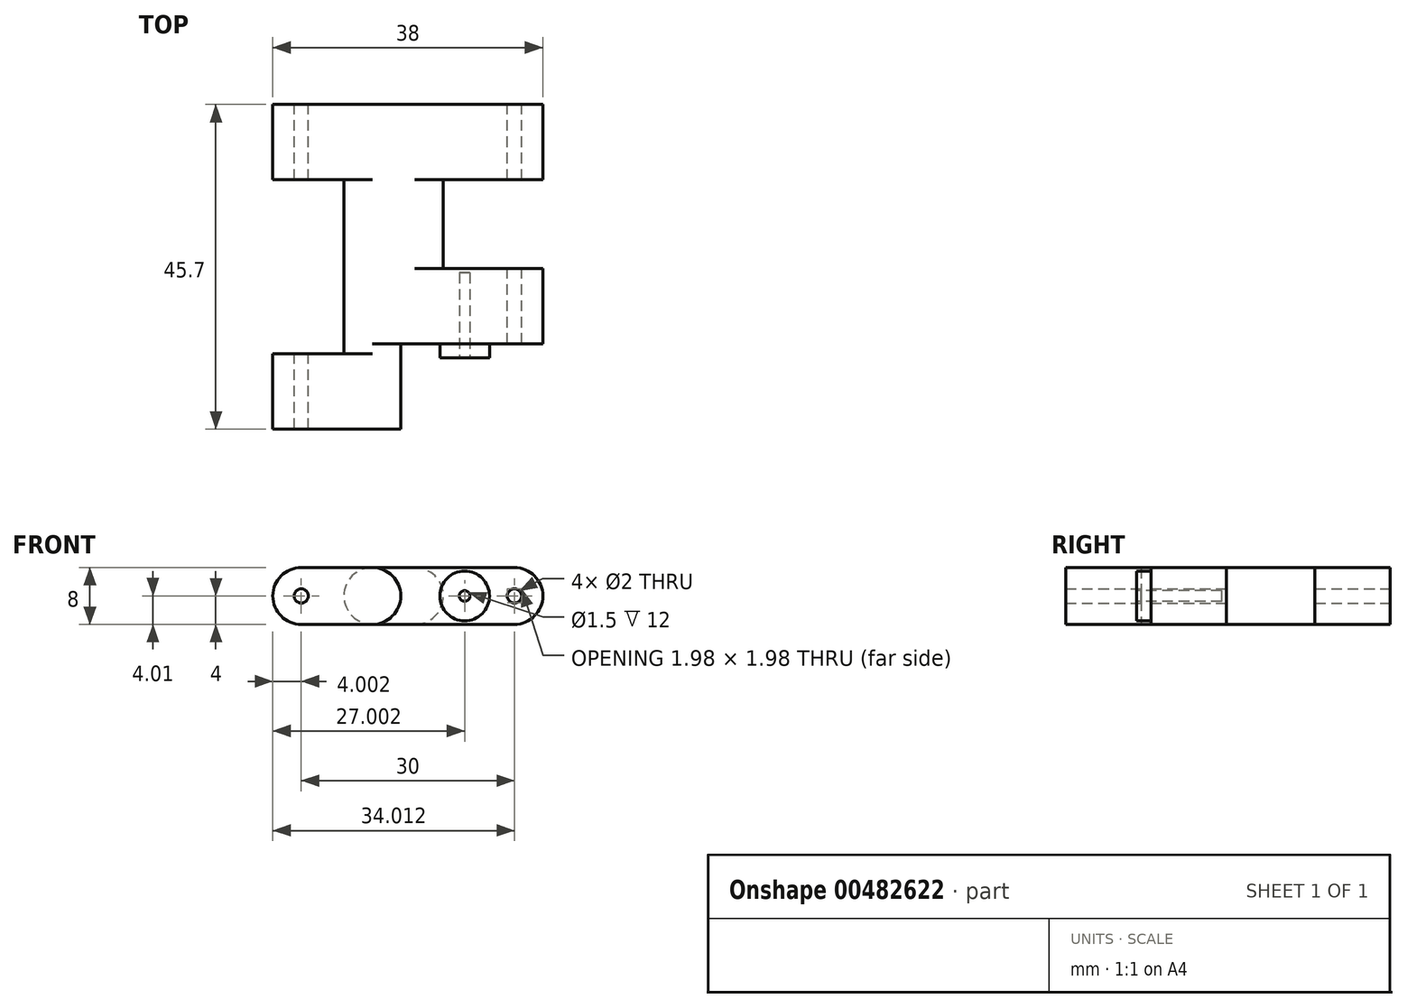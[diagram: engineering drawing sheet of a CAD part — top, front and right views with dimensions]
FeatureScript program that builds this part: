
annotation { "Feature Type Name" : "Feature", "Feature Type Description" : "" }
export const myFeature = defineFeature(function(context is Context, id is Id, definition is map)
    precondition{}
    {
        {
            var Q0;
            Q0=qCreatedBy(makeId("Top.planeOp"),FACE);
            var sketch = newSketch(context, id + "F0", { "sketchPlane" : qUnion([Q0])});
            skLineSegment(sketch, "E0", {"start": v(-9.9, -12.52) * mm, "end": v(8.1, -12.52) * mm});
            skLineSegment(sketch, "E1", {"start": v(8.1, -12.52) * mm, "end": v(8.1, -0.52) * mm});
            skLineSegment(sketch, "E2", {"start": v(8.1, -0.52) * mm, "end": v(28.1, -0.52) * mm});
            skLineSegment(sketch, "E3", {"start": v(28.1, -0.52) * mm, "end": v(28.1, 10.08) * mm});
            skLineSegment(sketch, "E4", {"start": v(28.1, 10.08) * mm, "end": v(14.1, 10.08) * mm});
            skLineSegment(sketch, "E5", {"start": v(14.1, 10.08) * mm, "end": v(14.1, 22.58) * mm});
            skLineSegment(sketch, "E6", {"start": v(14.1, 22.58) * mm, "end": v(28.1, 22.58) * mm});
            skLineSegment(sketch, "E7", {"start": v(28.1, 22.58) * mm, "end": v(28.1, 33.18) * mm});
            skLineSegment(sketch, "E8", {"start": v(28.1, 33.18) * mm, "end": v(-9.9, 33.18) * mm});
            skLineSegment(sketch, "E9", {"start": v(-9.9, 33.18) * mm, "end": v(-9.9, 22.58) * mm});
            skLineSegment(sketch, "E10", {"start": v(-9.9, 22.58) * mm, "end": v(0.1, 22.58) * mm});
            skLineSegment(sketch, "E11", {"start": v(0.1, 22.58) * mm, "end": v(0.1, -1.92) * mm});
            skLineSegment(sketch, "E12", {"start": v(0.1, -1.92) * mm, "end": v(-9.9, -1.92) * mm});
            skLineSegment(sketch, "E13", {"start": v(-9.9, -1.92) * mm, "end": v(-9.9, -12.52) * mm});
            skSolve(sketch);
        }
        {
            var Q0;
            Q0=makeQuery(id+"F0.imprint","IMPRINT",FACE,{"disambiguationData":[TD([[makeQuery(id+"F0.imprint","IMPRINT",EDGE,{"derivedFrom":sQuery(id+"F0.wireOp",EDGE,"E0")}),1.0]])]});
            extrude(context, id + "F1", {"entities" : qUnion([Q0]), "depth" : 8 * mm});
        }
        {
            var Q0;
            Q0=makeQuery(id+"F1.opExtrude","CAP_EDGE",EDGE,{"disambiguationData":[OSD([sQuery(id+"F0.wireOp",EDGE,"E13")])],"isStart":false});
            var Q1;
            Q1=makeQuery(id+"F1.opExtrude","CAP_EDGE",EDGE,{"disambiguationData":[OSD([sQuery(id+"F0.wireOp",EDGE,"E13")])],"isStart":true});
            var Q2;
            Q2=makeQuery(id+"F1.opExtrude","CAP_EDGE",EDGE,{"disambiguationData":[OSD([sQuery(id+"F0.wireOp",EDGE,"E1")])],"isStart":false});
            var Q3;
            Q3=makeQuery(id+"F1.opExtrude","CAP_EDGE",EDGE,{"disambiguationData":[OSD([sQuery(id+"F0.wireOp",EDGE,"E1")])],"isStart":true});
            var Q4;
            Q4=makeQuery(id+"F1.opExtrude","CAP_EDGE",EDGE,{"disambiguationData":[OSD([sQuery(id+"F0.wireOp",EDGE,"E3")])],"isStart":false});
            var Q5;
            Q5=makeQuery(id+"F1.opExtrude","CAP_EDGE",EDGE,{"disambiguationData":[OSD([sQuery(id+"F0.wireOp",EDGE,"E3")])],"isStart":true});
            var Q6;
            Q6=makeQuery(id+"F1.opExtrude","CAP_EDGE",EDGE,{"disambiguationData":[OSD([sQuery(id+"F0.wireOp",EDGE,"E7")])],"isStart":false});
            var Q7;
            Q7=makeQuery(id+"F1.opExtrude","CAP_EDGE",EDGE,{"disambiguationData":[OSD([sQuery(id+"F0.wireOp",EDGE,"E7")])],"isStart":true});
            var Q8;
            Q8=makeQuery(id+"F1.opExtrude","CAP_EDGE",EDGE,{"disambiguationData":[OSD([sQuery(id+"F0.wireOp",EDGE,"E9")])],"isStart":false});
            var Q9;
            Q9=makeQuery(id+"F1.opExtrude","CAP_EDGE",EDGE,{"disambiguationData":[OSD([sQuery(id+"F0.wireOp",EDGE,"E9")])],"isStart":true});
            fillet(context, id + "F2", {"entities" : qUnion([Q0, Q1, Q2, Q3, Q4, Q5, Q6, Q7, Q8, Q9]), "radius" : 4 * mm, "tangentPropagation" : true, "allowEdgeOverflow" : false});
        }
        {
            var Q0;
            Q0=makeQuery(id+"F1.opExtrude","SWEPT_FACE",FACE,{"disambiguationData":[OSD([sQuery(id+"F0.wireOp",EDGE,"E8")])]});
            var sketch = newSketch(context, id + "F3", { "sketchPlane" : qUnion([Q0])});
            skCircle(sketch, "E14", {"center": v(-24.1, 4) * mm, "radius": 1 * mm});
            skCircle(sketch, "E15", {"center": v(5.9, 4) * mm, "radius": 1 * mm});
            skSolve(sketch);
        }
        {
            var Q0;
            Q0 = qSketchRegion(id + "F3", true);
            extrude(context, id + "F4", {"entities" : qUnion([Q0]), "operationType" : NewBodyOperationType.REMOVE, "oppositeDirection" : true, "depth" : 60 * mm});
        }
        {
            var Q0;
            Q0=makeQuery(id+"F1.opExtrude","SWEPT_FACE",FACE,{"disambiguationData":[OSD([sQuery(id+"F0.wireOp",EDGE,"E2")])]});
            var sketch = newSketch(context, id + "F5", { "sketchPlane" : qUnion([Q0])});
            skCircle(sketch, "E16", {"center": v(17.1, 4) * mm, "radius": 3.5 * mm});
            skPoint(sketch, "E16.centerSnap0", {"position": v(28.1, 4) * mm});
            skSolve(sketch);
        }
        {
            var Q0;
            Q0=makeQuery(id+"F1.opExtrude","CAP_EDGE",EDGE,{"disambiguationData":[OSD([sQuery(id+"F0.wireOp",EDGE,"E11")])],"isStart":false});
            var Q1;
            Q1=makeQuery(id+"F1.opExtrude","CAP_EDGE",EDGE,{"disambiguationData":[OSD([sQuery(id+"F0.wireOp",EDGE,"E11")])],"isStart":true});
            var Q2;
            Q2=makeQuery(id+"F1.opExtrude","CAP_EDGE",EDGE,{"disambiguationData":[OSD([sQuery(id+"F0.wireOp",EDGE,"E5")])],"isStart":false});
            var Q3;
            Q3=makeQuery(id+"F1.opExtrude","CAP_EDGE",EDGE,{"disambiguationData":[OSD([sQuery(id+"F0.wireOp",EDGE,"E5")])],"isStart":true});
            fillet(context, id + "F6", {"entities" : qUnion([Q0, Q1, Q2, Q3]), "radius" : 4 * mm, "tangentPropagation" : true, "allowEdgeOverflow" : false});
        }
        {
            var Q0;
            Q0 = qSketchRegion(id + "F5", true);
            extrude(context, id + "F7", {"entities" : qUnion([Q0]), "operationType" : NewBodyOperationType.ADD, "depth" : 2 * mm});
        }
        {
            var Q0;
            Q0=makeQuery(id+"F7.opExtrude","CAP_FACE",FACE,{"disambiguationData":[OSD([sQuery(id+"F5.wireOp",EDGE,"E16")])],"isStart":false});
            var sketch = newSketch(context, id + "F8", { "sketchPlane" : qUnion([Q0])});
            skCircle(sketch, "E17", {"center": v(17.1, 4) * mm, "radius": 0.75 * mm});
            skSolve(sketch);
        }
        {
            var Q0;
            Q0=makeQuery(id+"F8.imprint","IMPRINT",FACE,{"disambiguationData":[TD([[makeQuery(id+"F8.imprint","IMPRINT",EDGE,{"derivedFrom":sQuery(id+"F8.wireOp",EDGE,"E17")}),1.0]])]});
            extrude(context, id + "F9", {"entities" : qUnion([Q0]), "operationType" : NewBodyOperationType.REMOVE, "oppositeDirection" : true, "depth" : 12 * mm});
        }
    });
